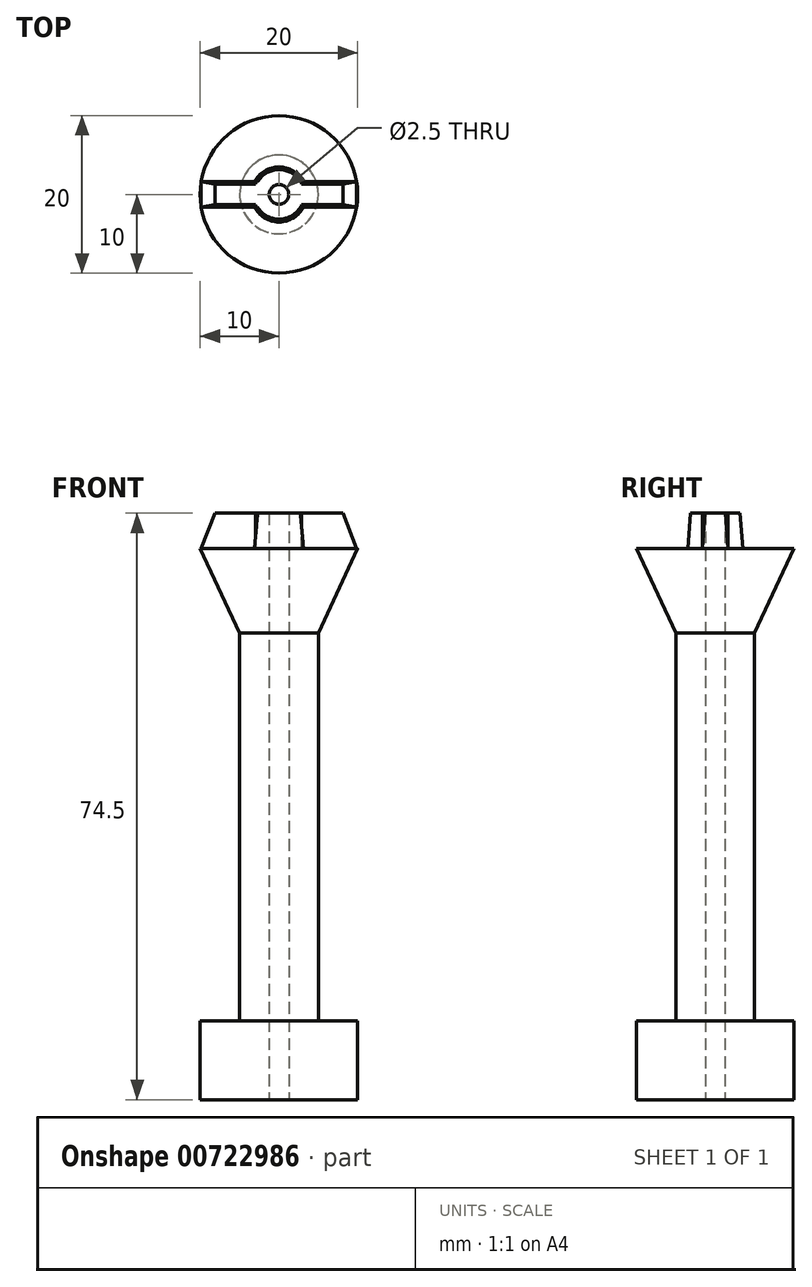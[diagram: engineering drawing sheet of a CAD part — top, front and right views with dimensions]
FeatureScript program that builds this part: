
annotation { "Feature Type Name" : "Feature", "Feature Type Description" : "" }
export const myFeature = defineFeature(function(context is Context, id is Id, definition is map)
    precondition{}
    {
        {
            var Q0;
            Q0=qCreatedBy(makeId("Front.planeOp"),FACE);
            var sketch = newSketch(context, id + "F0", { "sketchPlane" : qUnion([Q0])});
            skLineSegment(sketch, "E0", {"start": v(0, 0) * mm, "end": v(0, 108.49) * mm, "construction": true});
            skLineSegment(sketch, "E1", {"start": v(-1.25, 0) * mm, "end": v(-10, 0) * mm});
            skLineSegment(sketch, "E2", {"start": v(-10, 0) * mm, "end": v(-10, 10) * mm});
            skLineSegment(sketch, "E3", {"start": v(-10, 10) * mm, "end": v(-5, 10) * mm});
            skLineSegment(sketch, "E4", {"start": v(-5, 10) * mm, "end": v(-5, 59.28) * mm});
            skLineSegment(sketch, "E5", {"start": v(-25.35, 70) * mm, "end": v(42.65, 70) * mm, "construction": true});
            skLineSegment(sketch, "E6", {"start": v(-5, 59.28) * mm, "end": v(-10, 70) * mm});
            skLineSegment(sketch, "E7", {"start": v(0, 59.28) * mm, "end": v(-19.68, 59.28) * mm, "construction": true});
            skLineSegment(sketch, "E8", {"start": v(-10, 70) * mm, "end": v(-3.5, 70) * mm});
            skLineSegment(sketch, "E9", {"start": v(-1.25, 74.5) * mm, "end": v(-3.15, 74.5) * mm});
            skLineSegment(sketch, "E10", {"start": v(-3.15, 74.5) * mm, "end": v(-3.5, 70) * mm});
            skLineSegment(sketch, "E11", {"start": v(-1.25, 74.5) * mm, "end": v(-1.25, 0) * mm});
            skSolve(sketch);
        }
        {
            var Q0;
            Q0 = qSketchRegion(id + "F0", true);
            var Q1;
            Q1=sQuery(id+"F0.wireOp",EDGE,"E0");
            revolve(context, id + "F1", {"surfaceOperationType" : NewSurfaceOperationType.NEW, "entities" : qUnion([Q0]), "axis" : qUnion([Q1]), "revolveType" : RevolveType.FULL});
        }
        {
            var Q0;
            Q0=makeQuery(id+"F1.opRevolve","SWEPT_FACE",FACE,{"disambiguationData":[OSD([sQuery(id+"F0.wireOp",EDGE,"E8")])]});
            var sketch = newSketch(context, id + "F2", { "sketchPlane" : qUnion([Q0])});
            skLineSegment(sketch, "E12", {"start": v(-17.5, 0) * mm, "end": v(13.49, 0) * mm, "construction": true});
            skLineSegment(sketch, "E13", {"start": v(0, 3.5) * mm, "end": v(-14.3, 3.5) * mm, "construction": true});
            skLineSegment(sketch, "E14", {"start": v(0, 3.5) * mm, "end": v(9.9, 3.5) * mm, "construction": true});
            skLineSegment(sketch, "E15", {"start": v(-9.87, 1.6) * mm, "end": v(-3.11, 1.6) * mm});
            skArc(sketch, "E16.0", {"start": v(-9.87, -1.6) * mm, "mid": v(-10, 0) * mm, "end": v(-9.87, 1.6) * mm, "construction": true});
            skLineSegment(sketch, "E17.MirrorCS", {"start": v(-9.87, -1.6) * mm, "end": v(-3.11, -1.6) * mm});
            skLineSegment(sketch, "E18.trimOffspring", {"start": v(3.11, 1.6) * mm, "end": v(9.87, 1.6) * mm});
            skLineSegment(sketch, "E19.trimOffspring", {"start": v(3.11, -1.6) * mm, "end": v(9.87, -1.6) * mm});
            skArc(sketch, "E20.trimOffspring", {"start": v(9.87, 1.6) * mm, "mid": v(10, 0) * mm, "end": v(9.87, -1.6) * mm, "construction": true});
            skArc(sketch, "E21.0.0", {"start": v(-9.87, 1.6) * mm, "mid": v(-10, 0) * mm, "end": v(-9.87, -1.6) * mm});
            skArc(sketch, "E22.trimOffspring", {"start": v(9.87, -1.6) * mm, "mid": v(10, 0) * mm, "end": v(9.87, 1.6) * mm});
            skArc(sketch, "E23.0", {"start": v(2.71, 1.6) * mm, "mid": v(3.15, 0) * mm, "end": v(2.71, -1.6) * mm});
            skArc(sketch, "E24.0.0", {"start": v(-2.71, 1.6) * mm, "mid": v(-3.15, 0) * mm, "end": v(-2.71, -1.6) * mm});
            skLineSegment(sketch, "E25", {"start": v(-3.11, 1.6) * mm, "end": v(-2.71, 1.6) * mm});
            skLineSegment(sketch, "E26", {"start": v(-3.11, -1.6) * mm, "end": v(-2.71, -1.6) * mm});
            skLineSegment(sketch, "E27", {"start": v(3.11, 1.6) * mm, "end": v(2.71, 1.6) * mm});
            skLineSegment(sketch, "E28", {"start": v(3.11, -1.6) * mm, "end": v(2.71, -1.6) * mm});
            skArc(sketch, "E29.trimOffspring", {"start": v(2.71, -1.6) * mm, "mid": v(3.15, 0) * mm, "end": v(2.71, 1.6) * mm});
            skArc(sketch, "E30.trimOffspring", {"start": v(-2.71, -1.6) * mm, "mid": v(-3.15, 0) * mm, "end": v(-2.71, 1.6) * mm});
            skSolve(sketch);
        }
        {
            var Q0;
            Q0 = qSketchRegion(id + "F2", true);
            extrude(context, id + "F3", {"entities" : qUnion([Q0]), "operationType" : NewBodyOperationType.ADD, "depth" : 4.5 * mm, "offsetDistance" : 25 * mm});
        }
        {
            var Q0;
            Q0=qCreatedBy(makeId("Right.planeOp"),FACE);
            cPlane(context, id + "F4", {"entities" : qUnion([Q0]), "cplaneType" : CPlaneType.OFFSET, "offset" : 10.7 * mm, "width" : 150 * mm, "height" : 150 * mm});
        }
        {
            var Q0;
            Q0=qCreatedBy(id+"F4.planeOp",FACE);
            var sketch = newSketch(context, id + "F5", { "sketchPlane" : qUnion([Q0])});
            skLineSegment(sketch, "E31.0", {"start": v(1.6, 70) * mm, "end": v(0, 70) * mm});
            skLineSegment(sketch, "E32", {"start": v(0, 70) * mm, "end": v(0, 75.43) * mm, "construction": true});
            skLineSegment(sketch, "E33.0", {"start": v(1.6, 74.5) * mm, "end": v(-1.6, 74.5) * mm, "construction": true});
            skLineSegment(sketch, "E34", {"start": v(-1.3, 74.5) * mm, "end": v(-1.6, 70) * mm});
            skLineSegment(sketch, "E35.MirrorCS", {"start": v(1.3, 74.5) * mm, "end": v(1.6, 70) * mm});
            skLineSegment(sketch, "E36", {"start": v(-1.3, 74.5) * mm, "end": v(-1.6, 74.5) * mm});
            skLineSegment(sketch, "E37", {"start": v(-1.6, 70) * mm, "end": v(-1.6, 74.5) * mm});
            skLineSegment(sketch, "E38", {"start": v(1.3, 74.5) * mm, "end": v(1.6, 74.5) * mm});
            skLineSegment(sketch, "E39", {"start": v(1.6, 70) * mm, "end": v(1.6, 74.5) * mm});
            skPoint(sketch, "E40.start.orphan", {"position": v(0, 74.5) * mm});
            skSolve(sketch);
        }
        {
            var Q0;
            Q0 = qSketchRegion(id + "F5", true);
            extrude(context, id + "F6", {"entities" : qUnion([Q0]), "operationType" : NewBodyOperationType.REMOVE, "oppositeDirection" : true, "depth" : 7.82 * mm, "offsetDistance" : 25 * mm});
        }
        {
            var Q0;
            Q0=qCreatedBy(makeId("Right.planeOp"),FACE);
            cPlane(context, id + "F7", {"entities" : qUnion([Q0]), "cplaneType" : CPlaneType.OFFSET, "offset" : 10.7 * mm, "oppositeDirection" : true, "width" : 150 * mm, "height" : 150 * mm});
        }
        {
            var Q0;
            Q0=qCreatedBy(id+"F7.planeOp",FACE);
            var sketch = newSketch(context, id + "F8", { "sketchPlane" : qUnion([Q0])});
            skLineSegment(sketch, "E41.0", {"start": v(-1.6, 74.5) * mm, "end": v(1.6, 74.5) * mm, "construction": true});
            skLineSegment(sketch, "E42.0", {"start": v(-1.6, 70) * mm, "end": v(1.6, 70) * mm, "construction": true});
            skLineSegment(sketch, "E43.0", {"start": v(1.6, 74.5) * mm, "end": v(1.6, 70) * mm, "construction": true});
            skLineSegment(sketch, "E44.0", {"start": v(-1.6, 74.5) * mm, "end": v(-1.6, 70) * mm, "construction": true});
            skLineSegment(sketch, "E45", {"start": v(0, 70) * mm, "end": v(0, 76.08) * mm, "construction": true});
            skLineSegment(sketch, "E46", {"start": v(1.6, 74.5) * mm, "end": v(1.3, 74.5) * mm});
            skLineSegment(sketch, "E47", {"start": v(1.3, 74.5) * mm, "end": v(1.6, 70) * mm});
            skLineSegment(sketch, "E48", {"start": v(1.6, 74.5) * mm, "end": v(1.6, 70) * mm});
            skLineSegment(sketch, "E49.MirrorCS", {"start": v(-1.6, 74.5) * mm, "end": v(-1.3, 74.5) * mm});
            skLineSegment(sketch, "E50.MirrorCS", {"start": v(-1.6, 74.5) * mm, "end": v(-1.6, 70) * mm});
            skLineSegment(sketch, "E51.MirrorCS", {"start": v(-1.3, 74.5) * mm, "end": v(-1.6, 70) * mm});
            skSolve(sketch);
        }
        {
            var Q0;
            Q0 = qSketchRegion(id + "F8", true);
            extrude(context, id + "F9", {"entities" : qUnion([Q0]), "operationType" : NewBodyOperationType.REMOVE, "depth" : 7.7 * mm, "offsetDistance" : 25 * mm});
        }
        {
            var Q0;
            Q0=qCreatedBy(makeId("Front.planeOp"),FACE);
            cPlane(context, id + "F10", {"entities" : qUnion([Q0]), "cplaneType" : CPlaneType.OFFSET, "offset" : 10 * mm, "width" : 150 * mm, "height" : 150 * mm});
        }
        {
            var Q0;
            Q0=qCreatedBy(id+"F10.planeOp",FACE);
            var sketch = newSketch(context, id + "F11", { "sketchPlane" : qUnion([Q0])});
            skLineSegment(sketch, "E52.0", {"start": v(9.87, 70) * mm, "end": v(-9.87, 70) * mm, "construction": true});
            skEllipticalArc(sketch, "E53.0", {"construction": true});
            skEllipticalArc(sketch, "E54.0", {"construction": true});
            skLineSegment(sketch, "E55", {"start": v(-9.87, 70) * mm, "end": v(-7.95, 74.9) * mm});
            skLineSegment(sketch, "E56", {"start": v(-7.95, 74.9) * mm, "end": v(-10.55, 74.9) * mm});
            skLineSegment(sketch, "E57", {"start": v(-10.55, 74.9) * mm, "end": v(-10.26, 70) * mm});
            skLineSegment(sketch, "E58", {"start": v(-10.26, 70) * mm, "end": v(-9.87, 70) * mm});
            skPoint(sketch, "E59.0", {"position": v(0, 74.5) * mm});
            skLineSegment(sketch, "E60", {"start": v(0, 69.26) * mm, "end": v(0, 76.68) * mm, "construction": true});
            skPoint(sketch, "E60.startSnap0", {"position": v(0, 70) * mm});
            skLineSegment(sketch, "E61.MirrorCS", {"start": v(9.87, 70) * mm, "end": v(7.95, 74.9) * mm});
            skLineSegment(sketch, "E62.MirrorCS", {"start": v(7.95, 74.9) * mm, "end": v(10.55, 74.9) * mm});
            skLineSegment(sketch, "E63.MirrorCS", {"start": v(10.55, 74.9) * mm, "end": v(10.26, 70) * mm});
            skLineSegment(sketch, "E64.MirrorCS", {"start": v(10.26, 70) * mm, "end": v(9.87, 70) * mm});
            const initialGuessF11  = {"E53.0": [0, 0.094, 0, -1, 0.15, 0.01, 1.410105673842985, 1.44042734709175], "E54.0": [0, 0.094, 0, -1, 0.15, 0.01, 4.8427579600878365, 4.8730796333366015]};
            skSetInitialGuess(sketch, initialGuessF11);
            skSolve(sketch);
        }
        {
            var Q0;
            Q0 = qSketchRegion(id + "F11", true);
            extrude(context, id + "F12", {"entities" : qUnion([Q0]), "operationType" : NewBodyOperationType.REMOVE, "oppositeDirection" : true, "depth" : 25 * mm, "offsetDistance" : 25 * mm});
        }
    });
